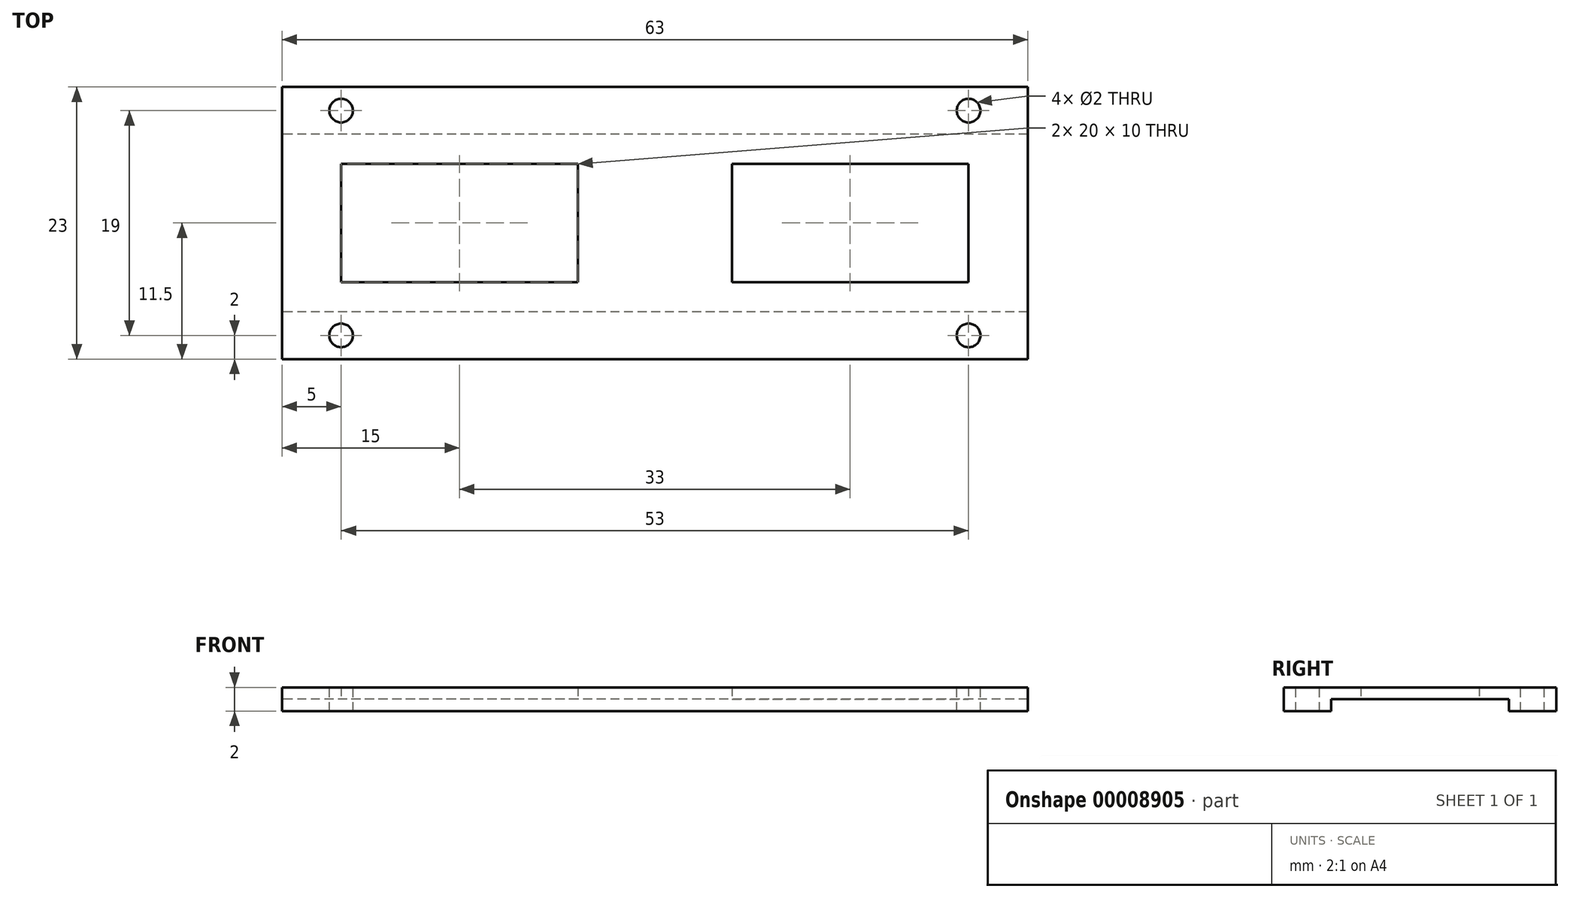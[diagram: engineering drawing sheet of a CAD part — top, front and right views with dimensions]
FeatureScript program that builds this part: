
annotation { "Feature Type Name" : "Feature", "Feature Type Description" : "" }
export const myFeature = defineFeature(function(context is Context, id is Id, definition is map)
    precondition{}
    {
        {
            var Q0;
            Q0=qCreatedBy(makeId("Top.planeOp"),FACE);
            var sketch = newSketch(context, id + "F0", { "sketchPlane" : qUnion([Q0])});
            skLineSegment(sketch, "E0.0", {"start": v(0, 12) * mm, "end": v(-32, 12) * mm, "construction": true});
            skLineSegment(sketch, "E1.0", {"start": v(0, 12) * mm, "end": v(32, 12) * mm, "construction": true});
            skLineSegment(sketch, "E2.0", {"start": v(0, -12) * mm, "end": v(-32, -12) * mm, "construction": true});
            skLineSegment(sketch, "E3.0", {"start": v(0, -12) * mm, "end": v(32, -12) * mm, "construction": true});
            skLineSegment(sketch, "E4", {"start": v(-32, 12) * mm, "end": v(-32, -12) * mm, "construction": true});
            skLineSegment(sketch, "E5", {"start": v(32, 12) * mm, "end": v(32, -12) * mm, "construction": true});
            skCircle(sketch, "E6", {"center": v(0, 0) * mm, "radius": 10 * mm, "construction": true});
            skLineSegment(sketch, "E7", {"start": v(0, 0) * mm, "end": v(-20, 0) * mm, "construction": true});
            skLineSegment(sketch, "E8", {"start": v(0, 0) * mm, "end": v(20, 0) * mm, "construction": true});
            skCircle(sketch, "E9", {"center": v(-20, 0) * mm, "radius": 10 * mm, "construction": true});
            skCircle(sketch, "E10", {"center": v(20, 0) * mm, "radius": 10 * mm, "construction": true});
            skLineSegment(sketch, "E11.0", {"start": v(-31.5, 12) * mm, "end": v(-31.5, -12) * mm});
            skLineSegment(sketch, "E12.0", {"start": v(31.5, 12) * mm, "end": v(31.5, -12) * mm});
            skLineSegment(sketch, "E13.0", {"start": v(0, 11.5) * mm, "end": v(32, 11.5) * mm});
            skLineSegment(sketch, "E14.0", {"start": v(0, 11.5) * mm, "end": v(-32, 11.5) * mm});
            skLineSegment(sketch, "E15.0", {"start": v(0, -11.5) * mm, "end": v(32, -11.5) * mm});
            skLineSegment(sketch, "E16.0", {"start": v(0, -11.5) * mm, "end": v(-32, -11.5) * mm});
            skLineSegment(sketch, "E17.0", {"start": v(32, -5) * mm, "end": v(31.5, -5) * mm});
            skLineSegment(sketch, "E18.trimOffspring", {"start": v(-31.5, 5) * mm, "end": v(-32, 5) * mm});
            skLineSegment(sketch, "E19.trimOffspring", {"start": v(-8.08, -5) * mm, "end": v(-11.92, -5) * mm});
            skLineSegment(sketch, "E20.trimOffspring", {"start": v(-8.08, 5) * mm, "end": v(-11.92, 5) * mm});
            skLineSegment(sketch, "E21.trimOffspring", {"start": v(11.92, 5) * mm, "end": v(8.08, 5) * mm});
            skLineSegment(sketch, "E22.trimOffspring", {"start": v(11.92, -5) * mm, "end": v(8.08, -5) * mm});
            skCircle(sketch, "E23.0", {"center": v(-20, 0) * mm, "radius": 9.5 * mm});
            skCircle(sketch, "E24.0", {"center": v(0, 0) * mm, "radius": 9.5 * mm});
            skCircle(sketch, "E25.0", {"center": v(20, 0) * mm, "radius": 9.5 * mm});
            skSolve(sketch);
        }
        {
            var Q0;
            {var subQ13=sQuery(id+"F0.wireOp",EDGE,"E19.trimOffspring");Q0=makeQuery(id+"F0.imprint","IMPRINT",FACE,{"disambiguationData":[TD([[makeQuery(id+"F0.imprint","IMPRINT",EDGE,{"derivedFrom":subQ13}),1.0]])]});}
            var Q1;
            {var subQ0=sQuery(id+"F0.wireOp",EDGE,"E9");var subQ3=makeQuery(id+"F0.imprint","INTERSECT",VERTEX,{"derivedFrom":[subQ0,sQuery(id+"F0.wireOp",EDGE,"E20.trimOffspring")]});Q1=makeQuery(id+"F0.imprint","IMPRINT",FACE,{"disambiguationData":[TD([[makeQuery(id+"F0.imprint","IMPRINT",EDGE,{"disambiguationData":[TD([[subQ3,1.0]])],"derivedFrom":subQ0}),1.0]])]});}
            var Q2;
            {var subQ0=sQuery(id+"F0.wireOp",EDGE,"E20.trimOffspring");Q2=makeQuery(id+"F0.imprint","IMPRINT",FACE,{"disambiguationData":[TD([[makeQuery(id+"F0.imprint","IMPRINT",EDGE,{"derivedFrom":subQ0}),1.0]])]});}
            var Q3;
            {var subQ0=sQuery(id+"F0.wireOp",EDGE,"E19.trimOffspring");Q3=makeQuery(id+"F0.imprint","IMPRINT",FACE,{"disambiguationData":[TD([[makeQuery(id+"F0.imprint","IMPRINT",EDGE,{"derivedFrom":subQ0}),-1.0]])]});}
            var Q4;
            {var subQ0=sQuery(id+"F0.wireOp",EDGE,"E6");var subQ6=makeQuery(id+"F0.imprint","INTERSECT",VERTEX,{"derivedFrom":[subQ0,sQuery(id+"F0.wireOp",EDGE,"E21.trimOffspring")]});Q4=makeQuery(id+"F0.imprint","IMPRINT",FACE,{"disambiguationData":[TD([[makeQuery(id+"F0.imprint","IMPRINT",EDGE,{"disambiguationData":[TD([[subQ6,1.0]])],"derivedFrom":subQ0}),1.0]])]});}
            var Q5;
            {var subQ0=sQuery(id+"F0.wireOp",EDGE,"E21.trimOffspring");Q5=makeQuery(id+"F0.imprint","IMPRINT",FACE,{"disambiguationData":[TD([[makeQuery(id+"F0.imprint","IMPRINT",EDGE,{"derivedFrom":subQ0}),1.0]])]});}
            var Q6;
            {var subQ0=sQuery(id+"F0.wireOp",EDGE,"E22.trimOffspring");Q6=makeQuery(id+"F0.imprint","IMPRINT",FACE,{"disambiguationData":[TD([[makeQuery(id+"F0.imprint","IMPRINT",EDGE,{"derivedFrom":subQ0}),-1.0]])]});}
            var Q7;
            {var subQ0=sQuery(id+"F0.wireOp",EDGE,"E10");var subQ2=makeQuery(id+"F0.imprint","INTERSECT",VERTEX,{"derivedFrom":[subQ0,sQuery(id+"F0.wireOp",EDGE,"E21.trimOffspring")]});Q7=makeQuery(id+"F0.imprint","IMPRINT",FACE,{"disambiguationData":[TD([[makeQuery(id+"F0.imprint","IMPRINT",EDGE,{"disambiguationData":[TD([[subQ2,-1.0]])],"derivedFrom":subQ0}),1.0]])]});}
            var Q8;
            {var subQ0=sQuery(id+"F0.wireOp",EDGE,"E23.0");var subQ2=makeQuery(id+"F0.imprint","INTERSECT",VERTEX,{"derivedFrom":[sQuery(id+"F0.wireOp",EDGE,"E19.trimOffspring"),subQ0]});Q8=makeQuery(id+"F0.imprint","IMPRINT",FACE,{"disambiguationData":[TD([[makeQuery(id+"F0.imprint","IMPRINT",EDGE,{"disambiguationData":[TD([[subQ2,1.0]])],"derivedFrom":subQ0}),1.0]])]});}
            var Q9;
            {var subQ0=sQuery(id+"F0.wireOp",EDGE,"E24.0");var subQ4=makeQuery(id+"F0.imprint","INTERSECT",VERTEX,{"derivedFrom":[sQuery(id+"F0.wireOp",EDGE,"E20.trimOffspring"),subQ0]});Q9=makeQuery(id+"F0.imprint","IMPRINT",FACE,{"disambiguationData":[TD([[makeQuery(id+"F0.imprint","IMPRINT",EDGE,{"disambiguationData":[TD([[subQ4,1.0]])],"derivedFrom":subQ0}),1.0]])]});}
            var Q10;
            {var subQ0=sQuery(id+"F0.wireOp",EDGE,"E25.0");var subQ2=makeQuery(id+"F0.imprint","INTERSECT",VERTEX,{"derivedFrom":[sQuery(id+"F0.wireOp",EDGE,"E21.trimOffspring"),subQ0]});Q10=makeQuery(id+"F0.imprint","IMPRINT",FACE,{"disambiguationData":[TD([[makeQuery(id+"F0.imprint","IMPRINT",EDGE,{"disambiguationData":[TD([[subQ2,-1.0]])],"derivedFrom":subQ0}),1.0]])]});}
            extrude(context, id + "F1", {"entities" : qUnion([Q0, Q1, Q2, Q3, Q4, Q5, Q6, Q7, Q8, Q9, Q10]), "depth" : 2 * mm});
        }
        {
            var Q0;
            Q0=makeQuery(id+"F1.opExtrude","CAP_FACE",FACE,{"disambiguationData":[OSD([sQuery(id+"F0.wireOp",EDGE,"E11.0"),sQuery(id+"F0.wireOp",EDGE,"E12.0"),sQuery(id+"F0.wireOp",EDGE,"E13.0"),sQuery(id+"F0.wireOp",EDGE,"E14.0"),sQuery(id+"F0.wireOp",EDGE,"E15.0"),sQuery(id+"F0.wireOp",EDGE,"E16.0")])],"isStart":true});
            var sketch = newSketch(context, id + "F2", { "sketchPlane" : qUnion([Q0])});
            skLineSegment(sketch, "E26.0", {"start": v(31.5, 7.5) * mm, "end": v(-31.5, 7.5) * mm});
            skLineSegment(sketch, "E27.0", {"start": v(31.5, -7.5) * mm, "end": v(-31.5, -7.5) * mm});
            skSolve(sketch);
        }
        {
            var Q0;
            {var subQ2=sQuery(id+"F2.wireOp",EDGE,"E26.0");Q0=makeQuery(id+"F2.imprint","IMPRINT",FACE,{"disambiguationData":[TD([[makeQuery(id+"F2.imprint","IMPRINT",EDGE,{"derivedFrom":subQ2}),1.0]])]});}
            extrude(context, id + "F3", {"entities" : qUnion([Q0]), "operationType" : NewBodyOperationType.REMOVE, "oppositeDirection" : true, "depth" : 1 * mm});
        }
        {
            var Q0;
            Q0=makeQuery(id+"F3.boolean.opBoolean","COPY",FACE,{"derivedFrom":makeQuery(id+"F3.opExtrude","CAP_FACE",FACE,{"disambiguationData":[OSD([sQuery(id+"F0.wireOp",EDGE,"E11.0"),sQuery(id+"F0.wireOp",EDGE,"E12.0"),sQuery(id+"F2.wireOp",EDGE,"E26.0"),sQuery(id+"F2.wireOp",EDGE,"E27.0")])],"isStart":false})});
            var sketch = newSketch(context, id + "F4", { "sketchPlane" : qUnion([Q0])});
            skLineSegment(sketch, "E28", {"start": v(0, 0) * mm, "end": v(-31.5, 0) * mm});
            skLineSegment(sketch, "E29", {"start": v(0, 0) * mm, "end": v(31.5, 0) * mm});
            skLineSegment(sketch, "E30.0", {"start": v(0, 5) * mm, "end": v(-31.5, 5) * mm});
            skLineSegment(sketch, "E31.0", {"start": v(0, -5) * mm, "end": v(-31.5, -5) * mm});
            skLineSegment(sketch, "E32", {"start": v(-31.5, 5) * mm, "end": v(-31.5, -5) * mm});
            skLineSegment(sketch, "E33.0", {"start": v(-26.5, 5) * mm, "end": v(-26.5, -5) * mm});
            skLineSegment(sketch, "E34.0", {"start": v(-6.5, 5) * mm, "end": v(-6.5, -5) * mm});
            skLineSegment(sketch, "E35.0", {"start": v(0, -5) * mm, "end": v(31.5, -5) * mm});
            skLineSegment(sketch, "E36.0", {"start": v(0, 5) * mm, "end": v(31.5, 5) * mm});
            skLineSegment(sketch, "E37", {"start": v(31.5, -5) * mm, "end": v(31.5, 5) * mm});
            skLineSegment(sketch, "E38.0", {"start": v(26.5, -5) * mm, "end": v(26.5, 5) * mm});
            skLineSegment(sketch, "E39.0", {"start": v(6.5, -5) * mm, "end": v(6.5, 5) * mm});
            skSolve(sketch);
        }
        {
            var Q0;
            {var subQ0=sQuery(id+"F4.wireOp",EDGE,"E34.0");var subQ1=sQuery(id+"F4.wireOp",EDGE,"E28");var subQ2=makeQuery(id+"F4.imprint","INTERSECT",VERTEX,{"derivedFrom":[subQ1,subQ0]});Q0=makeQuery(id+"F4.imprint","IMPRINT",FACE,{"disambiguationData":[TD([[makeQuery(id+"F4.imprint","IMPRINT",EDGE,{"disambiguationData":[TD([[subQ2,-1.0]])],"derivedFrom":subQ1}),1.0]])]});}
            var Q1;
            {var subQ0=sQuery(id+"F4.wireOp",EDGE,"E34.0");var subQ1=sQuery(id+"F4.wireOp",EDGE,"E28");var subQ2=makeQuery(id+"F4.imprint","INTERSECT",VERTEX,{"derivedFrom":[subQ1,subQ0]});Q1=makeQuery(id+"F4.imprint","IMPRINT",FACE,{"disambiguationData":[TD([[makeQuery(id+"F4.imprint","IMPRINT",EDGE,{"disambiguationData":[TD([[subQ2,-1.0]])],"derivedFrom":subQ1}),-1.0]])]});}
            var Q2;
            {var subQ0=sQuery(id+"F4.wireOp",EDGE,"E39.0");var subQ1=sQuery(id+"F4.wireOp",EDGE,"E29");var subQ2=makeQuery(id+"F4.imprint","INTERSECT",VERTEX,{"derivedFrom":[subQ1,subQ0]});Q2=makeQuery(id+"F4.imprint","IMPRINT",FACE,{"disambiguationData":[TD([[makeQuery(id+"F4.imprint","IMPRINT",EDGE,{"disambiguationData":[TD([[subQ2,-1.0]])],"derivedFrom":subQ1}),1.0]])]});}
            var Q3;
            {var subQ0=sQuery(id+"F4.wireOp",EDGE,"E39.0");var subQ1=sQuery(id+"F4.wireOp",EDGE,"E29");var subQ2=makeQuery(id+"F4.imprint","INTERSECT",VERTEX,{"derivedFrom":[subQ1,subQ0]});Q3=makeQuery(id+"F4.imprint","IMPRINT",FACE,{"disambiguationData":[TD([[makeQuery(id+"F4.imprint","IMPRINT",EDGE,{"disambiguationData":[TD([[subQ2,-1.0]])],"derivedFrom":subQ1}),-1.0]])]});}
            extrude(context, id + "F5", {"entities" : qUnion([Q0, Q1, Q2, Q3]), "operationType" : NewBodyOperationType.REMOVE, "oppositeDirection" : true, "depth" : 25 * mm});
        }
        {
            var Q0;
            Q0=makeQuery(id+"F1.opExtrude","CAP_FACE",FACE,{"disambiguationData":[OSD([sQuery(id+"F0.wireOp",EDGE,"E11.0"),sQuery(id+"F0.wireOp",EDGE,"E12.0"),sQuery(id+"F0.wireOp",EDGE,"E13.0"),sQuery(id+"F0.wireOp",EDGE,"E14.0"),sQuery(id+"F0.wireOp",EDGE,"E15.0"),sQuery(id+"F0.wireOp",EDGE,"E16.0")])],"isStart":false});
            var sketch = newSketch(context, id + "F6", { "sketchPlane" : qUnion([Q0])});
            skLineSegment(sketch, "E40", {"start": v(-31.5, -11.5) * mm, "end": v(-26.5, -11.5) * mm});
            skLineSegment(sketch, "E41", {"start": v(-31.5, 11.5) * mm, "end": v(-26.5, 11.5) * mm});
            skLineSegment(sketch, "E42", {"start": v(31.5, 11.5) * mm, "end": v(26.5, 11.5) * mm});
            skLineSegment(sketch, "E43", {"start": v(31.5, -11.5) * mm, "end": v(26.5, -11.5) * mm});
            skLineSegment(sketch, "E44.0", {"start": v(-31.5, 9.5) * mm, "end": v(-26.5, 9.5) * mm});
            skLineSegment(sketch, "E45.0", {"start": v(-31.5, -9.5) * mm, "end": v(-26.5, -9.5) * mm});
            skLineSegment(sketch, "E46.0", {"start": v(31.5, 9.5) * mm, "end": v(26.5, 9.5) * mm});
            skCircle(sketch, "E47", {"center": v(-26.5, 9.5) * mm, "radius": 1 * mm});
            skCircle(sketch, "E48", {"center": v(-26.5, -9.5) * mm, "radius": 1 * mm});
            skCircle(sketch, "E49", {"center": v(26.5, 9.5) * mm, "radius": 1 * mm});
            skLineSegment(sketch, "E50.0", {"start": v(31.5, -9.5) * mm, "end": v(26.5, -9.5) * mm});
            skCircle(sketch, "E51", {"center": v(26.5, -9.5) * mm, "radius": 1 * mm});
            skSolve(sketch);
        }
        {
            var Q0;
            Q0=makeQuery(id+"F6.imprint","IMPRINT",FACE,{"disambiguationData":[TD([[makeQuery(id+"F6.imprint","IMPRINT",EDGE,{"derivedFrom":sQuery(id+"F6.wireOp",EDGE,"E47")}),1.0]])]});
            var Q1;
            Q1=makeQuery(id+"F6.imprint","IMPRINT",FACE,{"disambiguationData":[TD([[makeQuery(id+"F6.imprint","IMPRINT",EDGE,{"derivedFrom":sQuery(id+"F6.wireOp",EDGE,"E48")}),1.0]])]});
            var Q2;
            Q2=makeQuery(id+"F6.imprint","IMPRINT",FACE,{"disambiguationData":[TD([[makeQuery(id+"F6.imprint","IMPRINT",EDGE,{"derivedFrom":sQuery(id+"F6.wireOp",EDGE,"E51")}),1.0]])]});
            var Q3;
            Q3=makeQuery(id+"F6.imprint","IMPRINT",FACE,{"disambiguationData":[TD([[makeQuery(id+"F6.imprint","IMPRINT",EDGE,{"derivedFrom":sQuery(id+"F6.wireOp",EDGE,"E49")}),1.0]])]});
            extrude(context, id + "F7", {"entities" : qUnion([Q0, Q1, Q2, Q3]), "operationType" : NewBodyOperationType.REMOVE, "oppositeDirection" : true, "depth" : 25 * mm});
        }
    });
